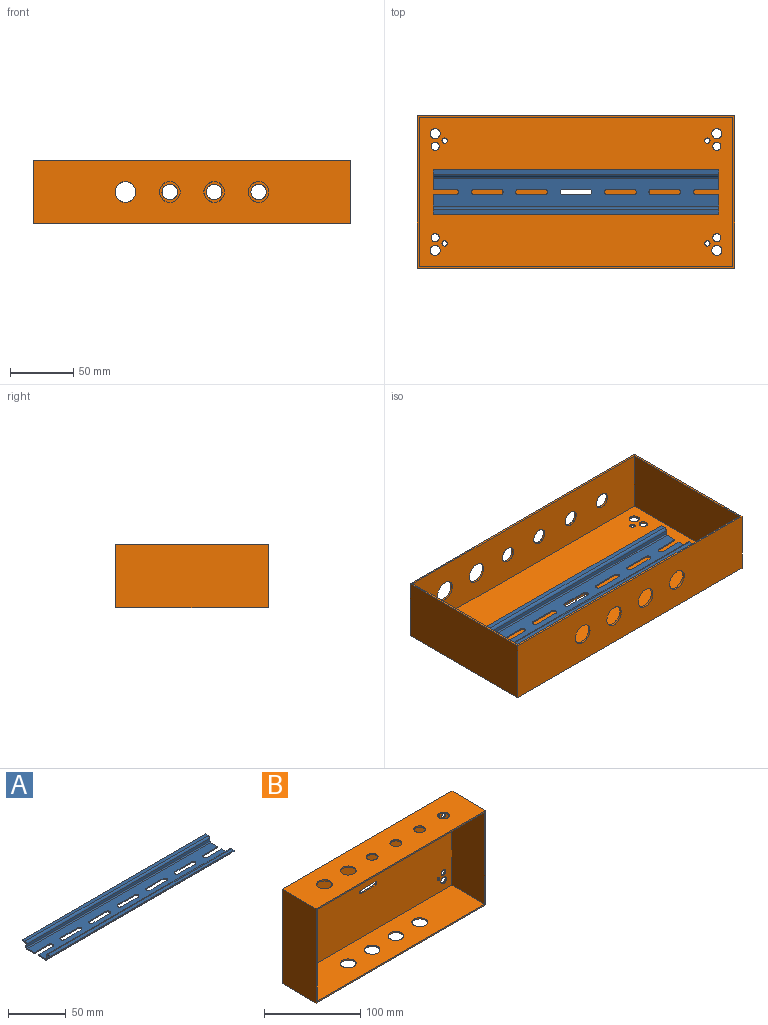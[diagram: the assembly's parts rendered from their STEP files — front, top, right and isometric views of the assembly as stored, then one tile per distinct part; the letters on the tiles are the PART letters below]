
ASSEMBLY  parts=2 mates=1
PART A: 50 faces, bbox 225x35x7 mm
  f0: plane 225x22mm, normal (0,0,-1), area 4233.6mm2, adj f2,f3,f6,f7,f22,f23,f24,f25
  f1: plane 225x22mm, normal (0,0,1), area 4233.6mm2, adj f2,f3,f15,f16,f22,f23,f24,f25
  f2: plane 15.25x7mm, normal (1,0,0), area 20mm2, adj f0,f1,f7,f8,f9,f10,f11,f12
  f3: plane 15.25x7mm, normal (-1,0,0), area 20mm2, adj f0,f1,f7,f8,f9,f10,f11,f12
  f4: cylinder r=1mm len=225mm, axis (-1,0,0), area 353.4mm2, adj f5,f21,f22,f23
  f5: plane 225x3mm, normal (0,-1,0), area 675mm2, adj f4,f6,f22,f23
  f6: cylinder r=2mm len=225mm, axis (-1,0,0), area 706.9mm2, adj f0,f5,f22,f23
  f7: cylinder r=2mm len=225mm, axis (-1,0,0), area 706.9mm2, adj f0,f2,f3,f8
  f8: plane 225x3mm, normal (0,1,0), area 675mm2, adj f2,f3,f7,f9
  f9: cylinder r=1mm len=225mm, axis (-1,0,0), area 353.4mm2, adj f2,f3,f8,f10
  f10: plane 225x3.5mm, normal (0,0,-1), area 787.5mm2, adj f2,f3,f9,f11
  f11: plane 225x1mm, normal (0,1,0), area 225mm2, adj f2,f3,f10,f12
  f12: plane 225x3.5mm, normal (0,0,1), area 787.5mm2, adj f2,f3,f11,f13
  f13: cylinder r=2mm len=225mm, axis (-1,0,0), area 706.9mm2, adj f2,f3,f12,f14
  f14: plane 225x3mm, normal (0,-1,0), area 675mm2, adj f2,f3,f13,f15
  f15: cylinder r=1mm len=225mm, axis (-1,0,0), area 353.4mm2, adj f1,f2,f3,f14
  f16: cylinder r=1mm len=225mm, axis (-1,0,0), area 353.4mm2, adj f1,f17,f22,f23
  f17: plane 225x3mm, normal (0,1,0), area 675mm2, adj f16,f18,f22,f23
  f18: cylinder r=2mm len=225mm, axis (-1,0,0), area 706.9mm2, adj f17,f19,f22,f23
  f19: plane 225x3.5mm, normal (0,0,1), area 787.5mm2, adj f18,f20,f22,f23
  f20: plane 225x1mm, normal (0,-1,0), area 225mm2, adj f19,f21,f22,f23
  f21: plane 225x3.5mm, normal (0,0,-1), area 787.5mm2, adj f4,f20,f22,f23
  f22: plane 15.25x7mm, normal (1,0,0), area 20mm2, adj f0,f1,f4,f5,f6,f16,f17,f18
  f23: plane 15.25x7mm, normal (-1,0,0), area 20mm2, adj f0,f1,f4,f5,f6,f16,f17,f18
  f24: cylinder r=2.25mm len=4.5mm, axis (0,0,-1), area 7.1mm2, adj f0,f1,f25,f26
  f25: plane 17.69x1mm, normal (0,1,0), area 17.7mm2, adj f0,f1,f23,f24
  f26: plane 17.69x1mm, normal (0,-1,0), area 17.7mm2, adj f0,f1,f3,f24
  f27: cylinder r=2.25mm len=4.5mm, axis (0,0,-1), area 7.1mm2, adj f0,f1,f28,f29
  f28: plane 17.81x1mm, normal (0,-1,0), area 17.8mm2, adj f0,f1,f2,f27
  f29: plane 17.81x1mm, normal (0,1,0), area 17.8mm2, adj f0,f1,f22,f27
  f30: cylinder r=2.25mm len=4.5mm, axis (0,0,-1), area 7.1mm2, adj f0,f1,f31,f33
  f31: plane 20.5x1mm, normal (0,1,0), area 20.5mm2, adj f0,f1,f30,f32
  f32: cylinder r=2.25mm len=4.5mm, axis (0,0,-1), area 7.1mm2, adj f0,f1,f31,f33
  f33: plane 20.5x1mm, normal (0,-1,0), area 20.5mm2, adj f0,f1,f30,f32
  f34: cylinder r=2.25mm len=4.5mm, axis (0,0,-1), area 7.1mm2, adj f0,f1,f35,f37
  f35: plane 20.5x1mm, normal (0,1,0), area 20.5mm2, adj f0,f1,f34,f36
  f36: cylinder r=2.25mm len=4.5mm, axis (0,0,-1), area 7.1mm2, adj f0,f1,f35,f37
  f37: plane 20.5x1mm, normal (0,-1,0), area 20.5mm2, adj f0,f1,f34,f36
  f38: cylinder r=2.25mm len=4.5mm, axis (0,0,-1), area 7.1mm2, adj f0,f1,f39,f41
  f39: plane 20.5x1mm, normal (0,1,0), area 20.5mm2, adj f0,f1,f38,f40
  f40: cylinder r=2.25mm len=4.5mm, axis (0,0,-1), area 7.1mm2, adj f0,f1,f39,f41
  f41: plane 20.5x1mm, normal (0,-1,0), area 20.5mm2, adj f0,f1,f38,f40
  f42: cylinder r=2.25mm len=4.5mm, axis (0,0,-1), area 7.1mm2, adj f0,f1,f43,f45
  f43: plane 20.5x1mm, normal (0,1,0), area 20.5mm2, adj f0,f1,f42,f44
  f44: cylinder r=2.25mm len=4.5mm, axis (0,0,-1), area 7.1mm2, adj f0,f1,f43,f45
  f45: plane 20.5x1mm, normal (0,-1,0), area 20.5mm2, adj f0,f1,f42,f44
  f46: cylinder r=2.25mm len=4.5mm, axis (0,0,-1), area 7.1mm2, adj f0,f1,f47,f49
  f47: plane 20.5x1mm, normal (0,1,0), area 20.5mm2, adj f0,f1,f46,f48
  f48: cylinder r=2.25mm len=4.5mm, axis (0,0,-1), area 7.1mm2, adj f0,f1,f47,f49
  f49: plane 20.5x1mm, normal (0,-1,0), area 20.5mm2, adj f0,f1,f46,f48
PART B: 37 faces, bbox 250x50x120 mm
  f0: cylinder r=2.25mm len=4.5mm, axis (0,1,0), area 11.3mm2, adj f1,f14,f21,f26
  f1: plane 20.5x1.6mm, normal (0,0,-1), area 32.8mm2, adj f0,f2,f21,f26
  f2: cylinder r=2.25mm len=4.5mm, axis (0,1,0), area 11.3mm2, adj f1,f14,f21,f26
  f3: cylinder r=3.2mm len=6.4mm, axis (0,1,0), area 32.2mm2, adj f21,f26
  f4: cylinder r=3.2mm len=6.4mm, axis (0,1,0), area 32.2mm2, adj f21,f26
  f5: cylinder r=3.2mm len=6.4mm, axis (0,1,0), area 32.2mm2, adj f21,f26
  f6: cylinder r=2.1mm len=4.2mm, axis (0,1,0), area 21.1mm2, adj f21,f26
  f7: cylinder r=2.1mm len=4.2mm, axis (0,1,0), area 21.1mm2, adj f21,f26
  f8: cylinder r=2.1mm len=4.2mm, axis (0,1,0), area 21.1mm2, adj f21,f26
  f9: cylinder r=2.1mm len=4.2mm, axis (0,1,0), area 21.1mm2, adj f21,f26
  f10: cylinder r=4mm len=8mm, axis (0,1,0), area 40.2mm2, adj f21,f26
  f11: cylinder r=4mm len=8mm, axis (0,1,0), area 40.2mm2, adj f21,f26
  f12: cylinder r=4mm len=8mm, axis (0,1,0), area 40.2mm2, adj f21,f26
  f13: cylinder r=4mm len=8mm, axis (0,1,0), area 40.2mm2, adj f21,f26
  f14: plane 20.5x1.6mm, normal (0,0,1), area 32.8mm2, adj f0,f2,f21,f26
  f15: cylinder r=3.2mm len=6.4mm, axis (0,1,0), area 32.2mm2, adj f21,f26
  f16: plane 250x120mm, normal (0,-1,0), area 1173.8mm2, adj f17,f18,f19,f20,f22,f23,f24,f25
  f17: plane 120x50mm, normal (1,0,0), area 6000mm2, adj f16,f18,f20,f21
  f18: plane 250x50mm, normal (0,0,1), area 11607.4mm2, adj f16,f17,f19,f21,f31,f32,f33,f34
  f19: plane 120x50mm, normal (-1,0,0), area 6000mm2, adj f16,f18,f20,f21
  f20: plane 250x50mm, normal (0,0,-1), area 11665.3mm2, adj f16,f17,f19,f21,f27,f28,f29,f30
  f21: plane 250x120mm, normal (0,1,0), area 29506.7mm2, adj f0,f1,f2,f3,f4,f5,f6,f7
  f22: plane 116.8x48.4mm, normal (-1,0,0), area 5653.1mm2, adj f16,f23,f25,f26
  f23: plane 246.8x48.4mm, normal (0,0,-1), area 11052.5mm2, adj f16,f22,f24,f26,f31,f32,f33,f34
  f24: plane 116.8x48.4mm, normal (1,0,0), area 5653.1mm2, adj f16,f23,f25,f26
  f25: plane 246.8x48.4mm, normal (0,0,1), area 11110.4mm2, adj f16,f22,f24,f26,f27,f28,f29,f30
  f26: plane 246.8x116.8mm, normal (0,-1,0), area 28332.9mm2, adj f0,f1,f2,f3,f4,f5,f6,f7
  f27: cylinder r=8.15mm len=16.3mm, axis (0,0,1), area 81.9mm2, adj f20,f25
  f28: cylinder r=8.15mm len=16.3mm, axis (0,0,1), area 81.9mm2, adj f20,f25
  f29: cylinder r=8.15mm len=16.3mm, axis (0,0,1), area 81.9mm2, adj f20,f25
  f30: cylinder r=8.15mm len=16.3mm, axis (0,0,1), area 81.9mm2, adj f20,f25
  f31: cylinder r=8.15mm len=16.3mm, axis (0,0,-1), area 81.9mm2, adj f18,f23
  f32: cylinder r=6.15mm len=12.3mm, axis (0,0,-1), area 61.8mm2, adj f18,f23
  f33: cylinder r=8.15mm len=16.3mm, axis (0,0,-1), area 81.9mm2, adj f18,f23
  f34: cylinder r=6.15mm len=12.3mm, axis (0,0,-1), area 61.8mm2, adj f18,f23
  f35: cylinder r=6.15mm len=12.3mm, axis (0,0,-1), area 61.8mm2, adj f18,f23
  f36: cylinder r=6.15mm len=12.3mm, axis (0,0,-1), area 61.8mm2, adj f18,f23
PLACE A t=(0.06,57.98,-46.4)mm
PLACE B rot(axis=(-1,0,0),90deg) t=(0,42.6,-24.4)mm
MATE fastened A.f42 <-> B.f0  axis (0,0,-1) through (-10.25,42.6,-22.8)mm
